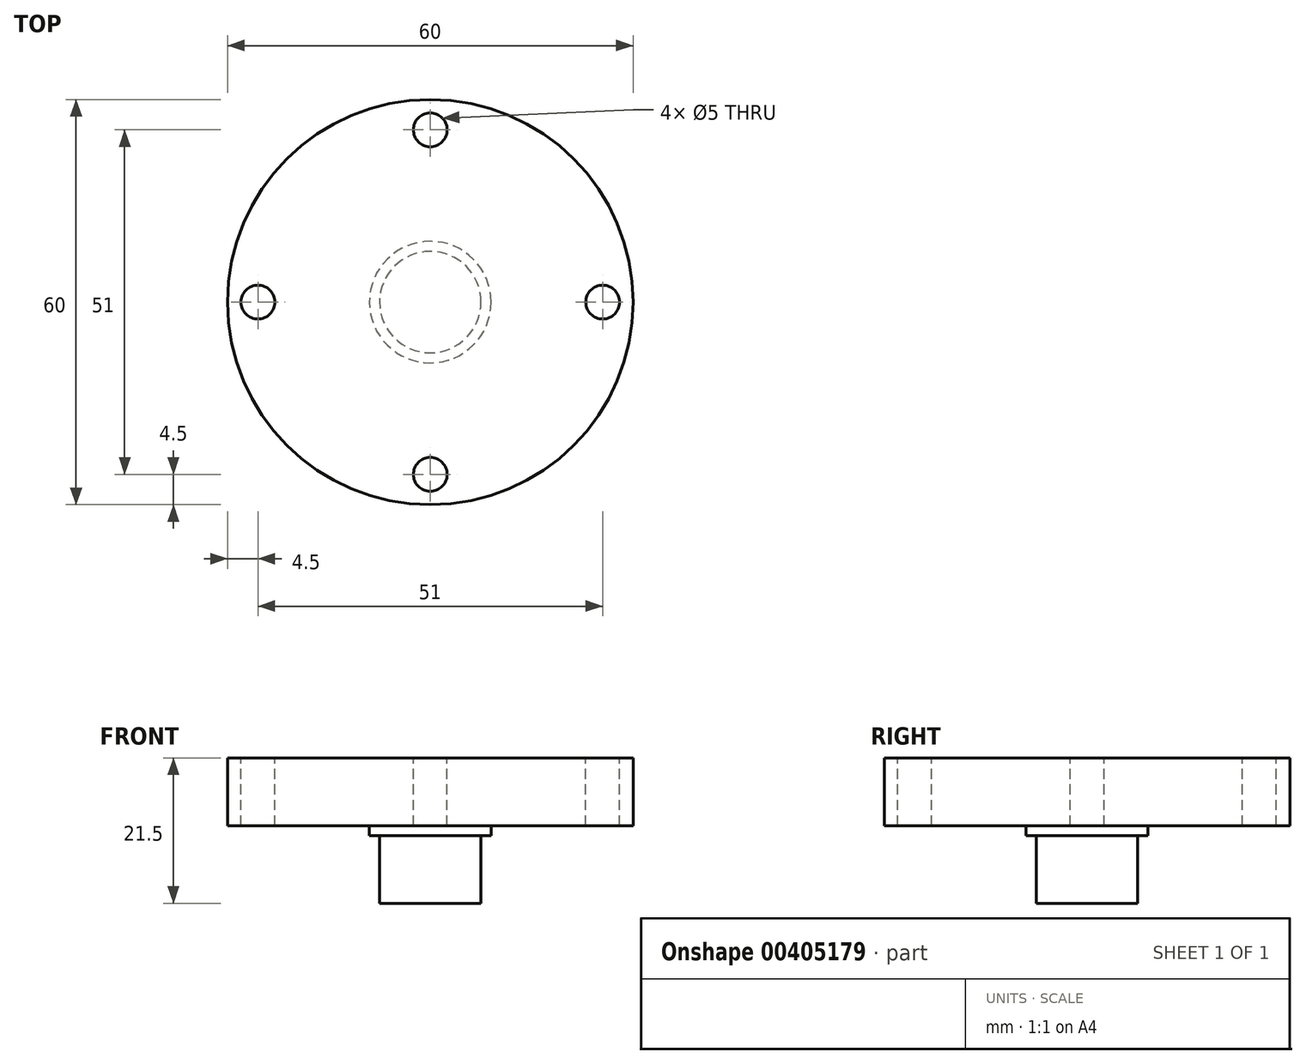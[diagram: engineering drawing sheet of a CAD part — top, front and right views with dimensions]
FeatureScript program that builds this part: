
annotation { "Feature Type Name" : "Feature", "Feature Type Description" : "" }
export const myFeature = defineFeature(function(context is Context, id is Id, definition is map)
    precondition{}
    {
        {
            var Q0;
            Q0=qCreatedBy(makeId("Top.planeOp"),FACE);
            var sketch = newSketch(context, id + "F0", { "sketchPlane" : qUnion([Q0])});
            skCircle(sketch, "E0", {"center": v(0, 0) * mm, "radius": 30 * mm});
            skSolve(sketch);
        }
        {
            var Q0;
            Q0 = qSketchRegion(id + "F0", true);
            extrude(context, id + "F1", {"entities" : qUnion([Q0]), "depth" : 10 * mm});
        }
        {
            var Q0;
            Q0=makeQuery(id+"F1.opExtrude","CAP_FACE",FACE,{"disambiguationData":[OSD([sQuery(id+"F0.wireOp",EDGE,"E0")])],"isStart":false});
            var sketch = newSketch(context, id + "F2", { "sketchPlane" : qUnion([Q0])});
            skLineSegment(sketch, "E1", {"start": v(0, 0) * mm, "end": v(0, 25.5) * mm});
            skCircle(sketch, "E2", {"center": v(0, 25.5) * mm, "radius": 2.5 * mm});
            skCircle(sketch, "E3.1.0", {"center": v(-25.5, 0) * mm, "radius": 2.5 * mm});
            skCircle(sketch, "E3.2.0", {"center": v(0, -25.5) * mm, "radius": 2.5 * mm});
            skCircle(sketch, "E3.3.0", {"center": v(25.5, 0) * mm, "radius": 2.5 * mm});
            skPoint(sketch, "E3.center", {"position": v(0, 0) * mm});
            skSolve(sketch);
        }
        {
            var Q0;
            Q0=makeQuery(id+"F2.imprint","IMPRINT",FACE,{"disambiguationData":[TD([[makeQuery(id+"F2.imprint","IMPRINT",EDGE,{"derivedFrom":sQuery(id+"F2.wireOp",EDGE,"E2")}),1.0]])]});
            var Q1;
            Q1=makeQuery(id+"F2.imprint","IMPRINT",FACE,{"disambiguationData":[TD([[makeQuery(id+"F2.imprint","IMPRINT",EDGE,{"derivedFrom":sQuery(id+"F2.wireOp",EDGE,"E3.3.0")}),1.0]])]});
            var Q2;
            Q2=makeQuery(id+"F2.imprint","IMPRINT",FACE,{"disambiguationData":[TD([[makeQuery(id+"F2.imprint","IMPRINT",EDGE,{"derivedFrom":sQuery(id+"F2.wireOp",EDGE,"E3.2.0")}),1.0]])]});
            var Q3;
            Q3=makeQuery(id+"F2.imprint","IMPRINT",FACE,{"disambiguationData":[TD([[makeQuery(id+"F2.imprint","IMPRINT",EDGE,{"derivedFrom":sQuery(id+"F2.wireOp",EDGE,"E3.1.0")}),1.0]])]});
            var Q4;
            Q4=sQuery(id+"F2.wireOp",EDGE,"E2");
            var Q5;
            Q5=sQuery(id+"F2.wireOp",EDGE,"E3.3.0");
            var Q6;
            Q6=sQuery(id+"F2.wireOp",EDGE,"E3.2.0");
            var Q7;
            Q7=sQuery(id+"F2.wireOp",EDGE,"E3.1.0");
            extrude(context, id + "F3", {"entities" : qUnion([Q0, Q1, Q2, Q3]), "operationType" : NewBodyOperationType.REMOVE, "surfaceEntities" : qUnion([Q4, Q5, Q6, Q7]), "endBound" : BoundingType.THROUGH_ALL, "oppositeDirection" : true, "depth" : 25 * mm});
        }
        {
            var Q0;
            Q0=makeQuery(id+"F1.opExtrude","CAP_FACE",FACE,{"disambiguationData":[OSD([sQuery(id+"F0.wireOp",EDGE,"E0")])],"isStart":true});
            var sketch = newSketch(context, id + "F4", { "sketchPlane" : qUnion([Q0])});
            skCircle(sketch, "E4", {"center": v(0, 0) * mm, "radius": 9 * mm});
            skSolve(sketch);
        }
        {
            var Q0;
            Q0 = qSketchRegion(id + "F4", true);
            extrude(context, id + "F5", {"entities" : qUnion([Q0]), "operationType" : NewBodyOperationType.ADD, "depth" : 1.5 * mm});
        }
        {
            var Q0;
            Q0=makeQuery(id+"F5.opExtrude","CAP_FACE",FACE,{"disambiguationData":[OSD([sQuery(id+"F4.wireOp",EDGE,"E4")])],"isStart":false});
            var sketch = newSketch(context, id + "F6", { "sketchPlane" : qUnion([Q0])});
            skCircle(sketch, "E5", {"center": v(0, 0) * mm, "radius": 7.5 * mm});
            skSolve(sketch);
        }
        {
            var Q0;
            Q0 = qSketchRegion(id + "F6", true);
            extrude(context, id + "F7", {"entities" : qUnion([Q0]), "operationType" : NewBodyOperationType.ADD, "depth" : 10 * mm});
        }
    });
